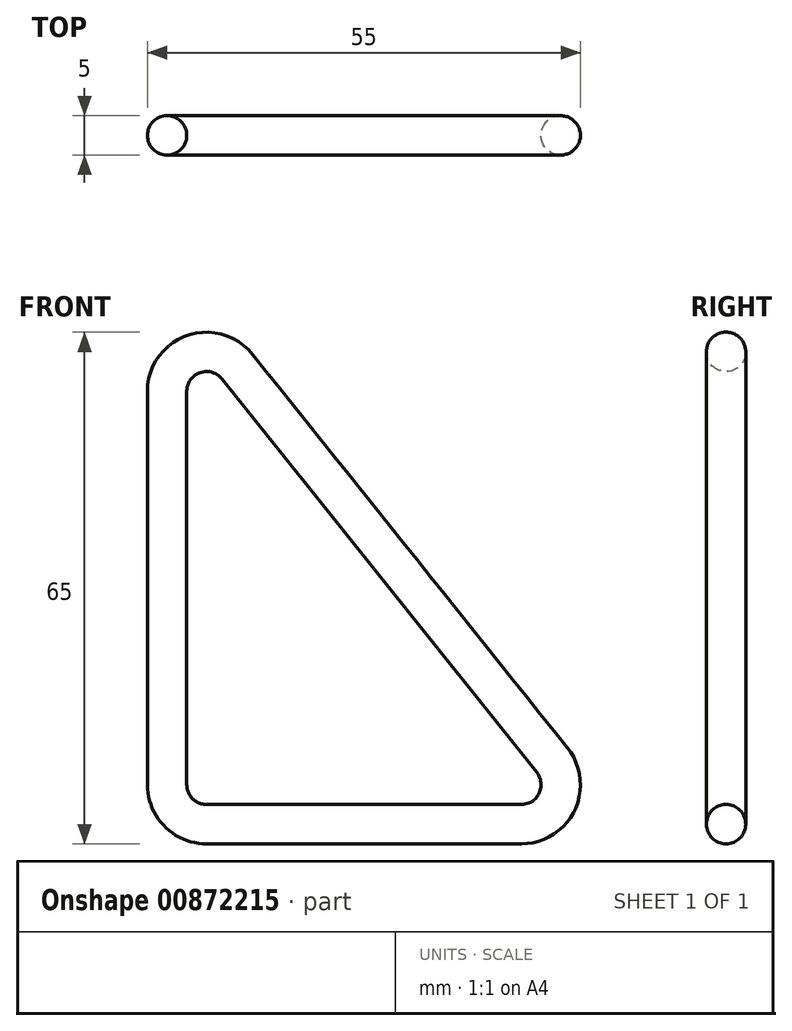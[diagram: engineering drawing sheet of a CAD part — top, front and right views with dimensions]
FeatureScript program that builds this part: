
annotation { "Feature Type Name" : "Feature", "Feature Type Description" : "" }
export const myFeature = defineFeature(function(context is Context, id is Id, definition is map)
    precondition{}
    {
        {
            var Q0;
            Q0=qCreatedBy(makeId("Front.planeOp"),FACE);
            var sketch = newSketch(context, id + "F0", { "sketchPlane" : qUnion([Q0])});
            skLineSegment(sketch, "E0", {"start": v(8.9, 58.12) * mm, "end": v(48.9, 8.12) * mm});
            skLineSegment(sketch, "E1", {"start": v(45, 0) * mm, "end": v(5, 0) * mm});
            skLineSegment(sketch, "E2", {"start": v(0, 5) * mm, "end": v(0, 55) * mm});
            skPoint(sketch, "E3.visualSharp", {"position": v(0, 69.25) * mm});
            skArc(sketch, "E3.filletArc", {"start": v(8.9, 58.12) * mm, "mid": v(3.34, 59.72) * mm, "end": v(0, 55) * mm});
            skPoint(sketch, "E4.visualSharp", {"position": v(55.4, 0) * mm});
            skArc(sketch, "E4.filletArc", {"start": v(45.11, 0) * mm, "mid": v(49.53, 2.89) * mm, "end": v(48.9, 8.12) * mm});
            skArc(sketch, "E5.filletArc", {"start": v(45, 0) * mm, "mid": v(49.5, 2.83) * mm, "end": v(48.9, 8.12) * mm});
            skPoint(sketch, "E6.visualSharp", {"position": v(0, 0) * mm});
            skArc(sketch, "E6.filletArc", {"start": v(0, 5) * mm, "mid": v(1.46, 1.46) * mm, "end": v(5, 0) * mm});
            skSolve(sketch);
        }
        {
            var Q0;
            Q0=qCreatedBy(makeId("Right.planeOp"),FACE);
            cPlane(context, id + "F1", {"entities" : qUnion([Q0]), "cplaneType" : CPlaneType.OFFSET, "offset" : 25 * mm, "width" : 150 * mm, "height" : 150 * mm});
        }
        {
            var Q0;
            Q0=qCreatedBy(id+"F1.planeOp",FACE);
            var sketch = newSketch(context, id + "F2", { "sketchPlane" : qUnion([Q0])});
            skCircle(sketch, "E7", {"center": v(0, 0) * mm, "radius": 2.5 * mm});
            skSolve(sketch);
        }
        {
            var Q0;
            Q0=makeQuery(id+"F2.imprint","IMPRINT",FACE,{"disambiguationData":[TD([[makeQuery(id+"F2.imprint","IMPRINT",EDGE,{"derivedFrom":sQuery(id+"F2.wireOp",EDGE,"E7")}),1.0]])]});
            var Q1;
            Q1=sQuery(id+"F0.wireOp",EDGE,"E1");
            var Q2;
            Q2=sQuery(id+"F0.wireOp",EDGE,"E5.filletArc");
            var Q3;
            Q3=sQuery(id+"F0.wireOp",EDGE,"E0");
            var Q4;
            Q4=sQuery(id+"F0.wireOp",EDGE,"E3.filletArc");
            var Q5;
            Q5=sQuery(id+"F0.wireOp",EDGE,"E2");
            var Q6;
            Q6=sQuery(id+"F0.wireOp",EDGE,"E6.filletArc");
            sweep(context, id + "F3", {"profiles" : qUnion([Q0]), "path" : qUnion([Q1, Q2, Q3, Q4, Q5, Q6])});
        }
    });
